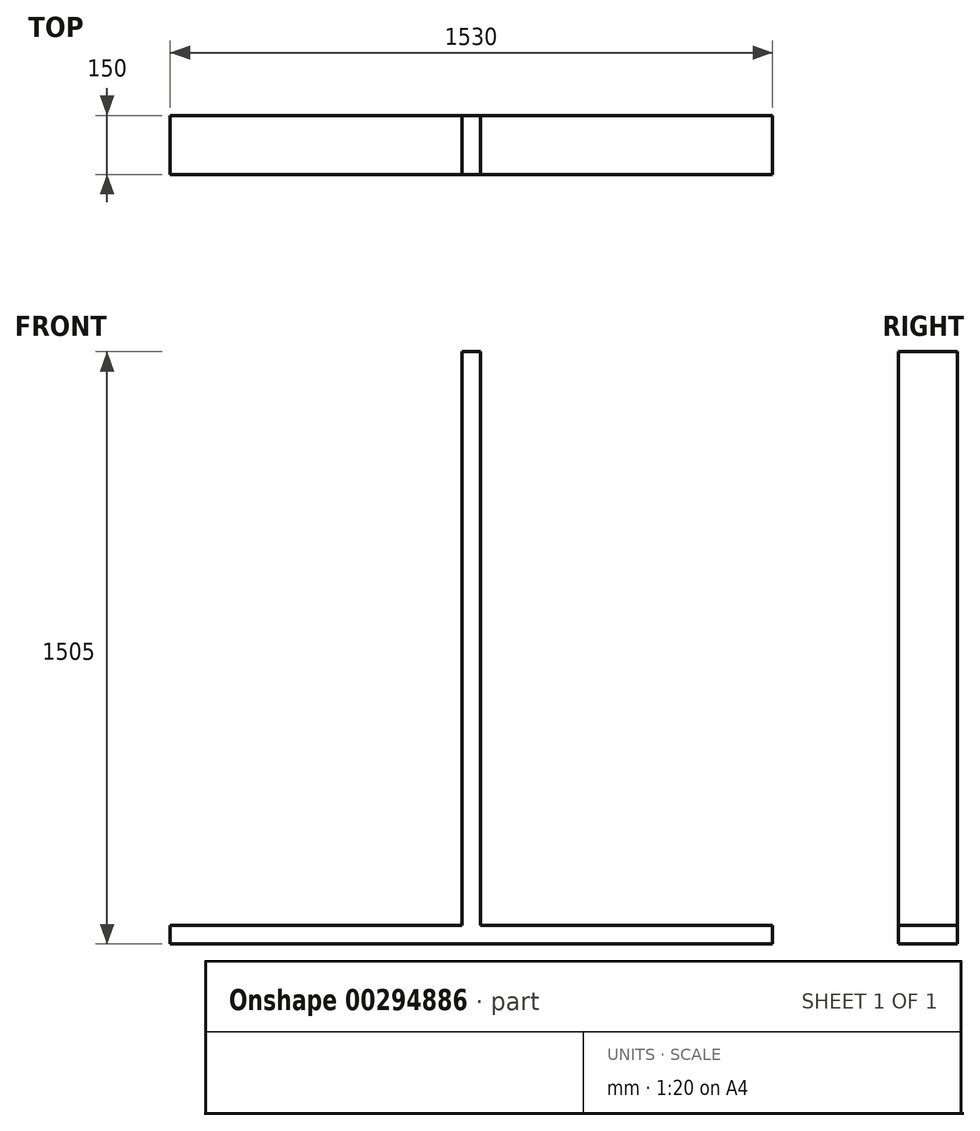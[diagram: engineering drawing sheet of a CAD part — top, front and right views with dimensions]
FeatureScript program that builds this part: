
annotation { "Feature Type Name" : "Feature", "Feature Type Description" : "" }
export const myFeature = defineFeature(function(context is Context, id is Id, definition is map)
    precondition{}
    {
        {
            var Q0;
            Q0=qCreatedBy(makeId("Front.planeOp"),FACE);
            var sketch = newSketch(context, id + "F0", { "sketchPlane" : qUnion([Q0])});
            skLineSegment(sketch, "E0", {"start": v(0, 1505) * mm, "end": v(0, 0) * mm, "construction": true});
            skLineSegment(sketch, "E1", {"start": v(0, 0) * mm, "end": v(765, 0) * mm});
            skLineSegment(sketch, "E2", {"start": v(765, 0) * mm, "end": v(765, 47) * mm});
            skLineSegment(sketch, "E3", {"start": v(765, 47) * mm, "end": v(23.5, 47) * mm});
            skLineSegment(sketch, "E4", {"start": v(23.5, 47) * mm, "end": v(23.5, 1505) * mm});
            skLineSegment(sketch, "E5", {"start": v(23.5, 1505) * mm, "end": v(0, 1505) * mm});
            skLineSegment(sketch, "E6.MirrorCS", {"start": v(-23.5, 1505) * mm, "end": v(0, 1505) * mm});
            skLineSegment(sketch, "E7.MirrorCS", {"start": v(-23.5, 47) * mm, "end": v(-23.5, 1505) * mm});
            skLineSegment(sketch, "E8.MirrorCS", {"start": v(-765, 47) * mm, "end": v(-23.5, 47) * mm});
            skLineSegment(sketch, "E9.MirrorCS", {"start": v(0, 0) * mm, "end": v(-765, 0) * mm});
            skLineSegment(sketch, "E10.MirrorCS", {"start": v(-765, 0) * mm, "end": v(-765, 47) * mm});
            skSolve(sketch);
        }
        {
            var Q0;
            Q0=makeQuery(id+"F0.imprint","IMPRINT",FACE,{"disambiguationData":[TD([[makeQuery(id+"F0.imprint","IMPRINT",EDGE,{"derivedFrom":sQuery(id+"F0.wireOp",EDGE,"E1")}),1.0]])]});
            extrude(context, id + "F1", {"entities" : qUnion([Q0]), "depth" : 150 * mm});
        }
    });
